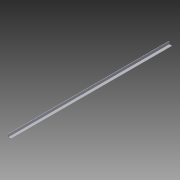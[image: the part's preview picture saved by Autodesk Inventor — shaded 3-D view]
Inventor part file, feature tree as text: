
AUTODESK INVENTOR PART (.ipt)
format: ipt  version: 2014 SP1 (Build 180222100, 222)  size: 77,312 bytes
history: native  units: in
note: dims shown in document units (in); Inventor stores cm internally (conversion verified against a paired STEP export)
features: extrude x1, sketch x1
ambient origin geometry x8: Origin, YZ Plane, XZ Plane, XY Plane, X Axis, Y Axis, Z Axis, Center Point
bodies: Solid1 (feature_tree)
feature tree (2):
  extrude  "Extrusion1"  Depth=0.0625in
  sketch  "Sketch1"  dims[d0=0.5in d1=0.0625in d2=0.5in d3=0.0625in d4=26.75in d5=0.0in]
